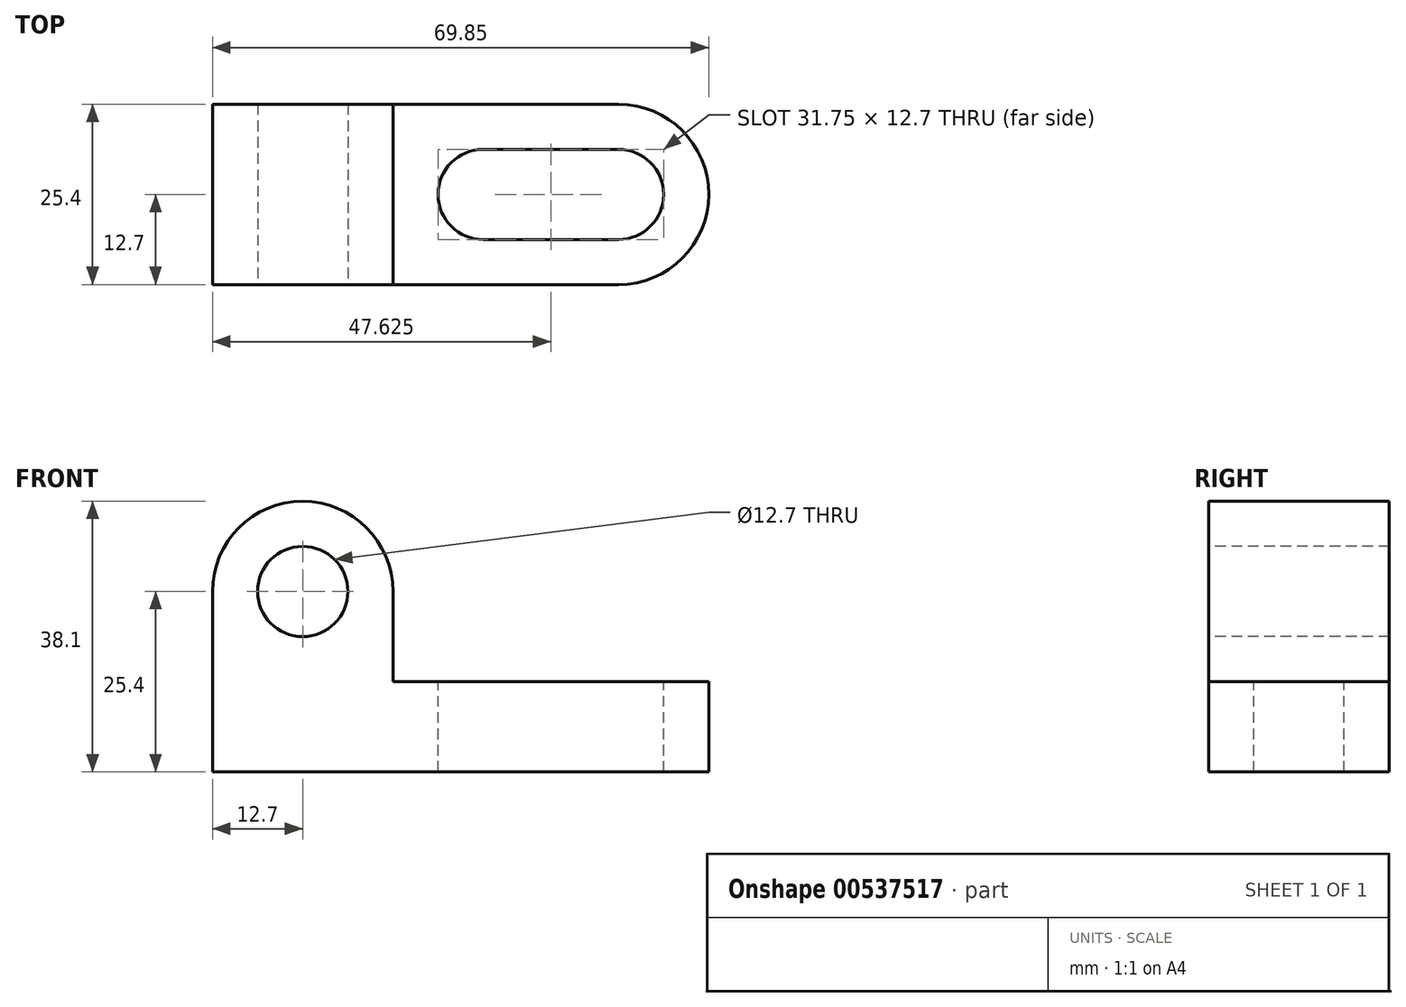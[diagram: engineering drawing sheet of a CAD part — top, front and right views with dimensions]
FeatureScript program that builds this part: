
annotation { "Feature Type Name" : "Feature", "Feature Type Description" : "" }
export const myFeature = defineFeature(function(context is Context, id is Id, definition is map)
    precondition{}
    {
        {
            var Q0;
            Q0=qCreatedBy(makeId("Front.planeOp"),FACE);
            var sketch = newSketch(context, id + "F0", { "sketchPlane" : qUnion([Q0])});
            skLineSegment(sketch, "E0", {"start": v(0, 0) * mm, "end": v(69.85, 0) * mm});
            skLineSegment(sketch, "E1", {"start": v(69.85, 0) * mm, "end": v(69.85, 38.1) * mm});
            skLineSegment(sketch, "E2", {"start": v(69.85, 38.1) * mm, "end": v(0, 38.1) * mm});
            skLineSegment(sketch, "E3", {"start": v(0, 38.1) * mm, "end": v(0, 0) * mm});
            skSolve(sketch);
        }
        {
            var Q0;
            Q0 = qSketchRegion(id + "F0", true);
            extrude(context, id + "F1", {"entities" : qUnion([Q0]), "depth" : 25.4 * mm, "offsetDistance" : 25.4 * mm});
        }
        {
            var Q0;
            Q0=makeQuery(id+"F1.opExtrude","CAP_FACE",FACE,{"disambiguationData":[OSD([sQuery(id+"F0.wireOp",EDGE,"E0"),sQuery(id+"F0.wireOp",EDGE,"E1"),sQuery(id+"F0.wireOp",EDGE,"E2"),sQuery(id+"F0.wireOp",EDGE,"E3")])],"isStart":false});
            var sketch = newSketch(context, id + "F2", { "sketchPlane" : qUnion([Q0])});
            skLineSegment(sketch, "E4", {"start": v(69.85, 0) * mm, "end": v(69.85, 12.7) * mm});
            skLineSegment(sketch, "E5", {"start": v(69.85, 12.7) * mm, "end": v(25.4, 12.7) * mm});
            skLineSegment(sketch, "E6", {"start": v(25.4, 12.7) * mm, "end": v(25.4, 38.1) * mm});
            skLineSegment(sketch, "E7", {"start": v(25.4, 38.1) * mm, "end": v(0, 38.1) * mm});
            skSolve(sketch);
        }
        {
            var Q0;
            Q0 = qSketchRegion(id + "F2", true);
            var Q1;
            {var subQ0=sQuery(id+"F2.wireOp",EDGE,"E5");Q1=makeQuery(id+"F2.imprint","IMPRINT",FACE,{"disambiguationData":[TD([[makeQuery(id+"F2.imprint","IMPRINT",EDGE,{"derivedFrom":subQ0}),-1.0]])]});}
            extrude(context, id + "F3", {"entities" : qUnion([Q0, Q1]), "operationType" : NewBodyOperationType.REMOVE, "oppositeDirection" : true, "depth" : 25.4 * mm, "offsetDistance" : 25.4 * mm});
        }
        {
            var Q0;
            Q0=makeQuery(id+"F1.opExtrude","CAP_FACE",FACE,{"disambiguationData":[OSD([sQuery(id+"F0.wireOp",EDGE,"E0"),sQuery(id+"F0.wireOp",EDGE,"E1"),sQuery(id+"F0.wireOp",EDGE,"E2"),sQuery(id+"F0.wireOp",EDGE,"E3")])],"isStart":false});
            var sketch = newSketch(context, id + "F4", { "sketchPlane" : qUnion([Q0])});
            skLineSegment(sketch, "E8", {"start": v(0, 38.1) * mm, "end": v(0, 25.4) * mm});
            skLineSegment(sketch, "E9", {"start": v(25.4, 38.1) * mm, "end": v(25.4, 25.4) * mm});
            skArc(sketch, "E10", {"start": v(25.4, 25.4) * mm, "mid": v(12.7, 38.1) * mm, "end": v(0, 25.4) * mm});
            skLineSegment(sketch, "E11", {"start": v(12.7, 38.1) * mm, "end": v(12.7, 31.75) * mm});
            skPoint(sketch, "E11.endSnap0", {"position": v(12.7, 38.1) * mm});
            skLineSegment(sketch, "E12", {"start": v(12.7, 0) * mm, "end": v(12.7, 19.05) * mm});
            skCircle(sketch, "E13", {"center": v(12.7, 25.4) * mm, "radius": 6.35 * mm});
            skSolve(sketch);
        }
        {
            var Q0;
            {var subQ0=sQuery(id+"F4.wireOp",EDGE,"E8");Q0=makeQuery(id+"F4.imprint","IMPRINT",FACE,{"disambiguationData":[TD([[makeQuery(id+"F4.imprint","IMPRINT",EDGE,{"derivedFrom":subQ0}),1.0]])]});}
            var Q1;
            {var subQ0=sQuery(id+"F4.wireOp",EDGE,"E9");Q1=makeQuery(id+"F4.imprint","IMPRINT",FACE,{"disambiguationData":[TD([[makeQuery(id+"F4.imprint","IMPRINT",EDGE,{"derivedFrom":subQ0}),1.0]])]});}
            var Q2;
            {var subQ0=sQuery(id+"F4.wireOp",EDGE,"E13");var subQ1=makeQuery(id+"F4.imprint","INTERSECT",VERTEX,{"derivedFrom":[sQuery(id+"F4.wireOp",EDGE,"E11"),subQ0]});Q2=makeQuery(id+"F4.imprint","IMPRINT",FACE,{"disambiguationData":[TD([[makeQuery(id+"F4.imprint","IMPRINT",EDGE,{"disambiguationData":[TD([[subQ1,-1.0]])],"derivedFrom":subQ0}),1.0]])]});}
            extrude(context, id + "F5", {"entities" : qUnion([Q0, Q1, Q2]), "operationType" : NewBodyOperationType.REMOVE, "oppositeDirection" : true, "depth" : 25.4 * mm, "offsetDistance" : 25.4 * mm});
        }
        {
            var Q0;
            Q0=makeQuery(id+"F3.boolean.opBoolean","COPY",FACE,{"derivedFrom":makeQuery(id+"F3.opExtrude","SWEPT_FACE",FACE,{"disambiguationData":[OSD([sQuery(id+"F2.wireOp",EDGE,"E5")])]})});
            var sketch = newSketch(context, id + "F6", { "sketchPlane" : qUnion([Q0])});
            skCircle(sketch, "E14", {"center": v(38.1, -12.7) * mm, "radius": 6.35 * mm});
            skCircle(sketch, "E15", {"center": v(57.15, -12.7) * mm, "radius": 6.35 * mm});
            skLineSegment(sketch, "E16", {"start": v(38.1, -6.35) * mm, "end": v(57.15, -6.35) * mm});
            skLineSegment(sketch, "E17", {"start": v(38.1, -19.05) * mm, "end": v(57.15, -19.05) * mm});
            skSolve(sketch);
        }
        {
            var Q0;
            {var subQ0=sQuery(id+"F6.wireOp",EDGE,"E14");var subQ1=makeQuery(id+"F6.imprint","INTERSECT",VERTEX,{"derivedFrom":[subQ0,sQuery(id+"F6.wireOp",EDGE,"E16")]});Q0=makeQuery(id+"F6.imprint","IMPRINT",FACE,{"disambiguationData":[TD([[makeQuery(id+"F6.imprint","IMPRINT",EDGE,{"disambiguationData":[TD([[subQ1,-1.0]])],"derivedFrom":subQ0}),1.0]])]});}
            var Q1;
            {var subQ0=sQuery(id+"F6.wireOp",EDGE,"E16");Q1=makeQuery(id+"F6.imprint","IMPRINT",FACE,{"disambiguationData":[TD([[makeQuery(id+"F6.imprint","IMPRINT",EDGE,{"derivedFrom":subQ0}),-1.0]])]});}
            var Q2;
            {var subQ0=sQuery(id+"F6.wireOp",EDGE,"E15");var subQ1=makeQuery(id+"F6.imprint","INTERSECT",VERTEX,{"derivedFrom":[subQ0,sQuery(id+"F6.wireOp",EDGE,"E16")]});Q2=makeQuery(id+"F6.imprint","IMPRINT",FACE,{"disambiguationData":[TD([[makeQuery(id+"F6.imprint","IMPRINT",EDGE,{"disambiguationData":[TD([[subQ1,-1.0]])],"derivedFrom":subQ0}),1.0]])]});}
            extrude(context, id + "F7", {"entities" : qUnion([Q0, Q1, Q2]), "operationType" : NewBodyOperationType.REMOVE, "oppositeDirection" : true, "depth" : 12.7 * mm, "offsetDistance" : 25.4 * mm});
        }
        {
            var Q0;
            Q0=makeQuery(id+"F3.boolean.opBoolean","COPY",FACE,{"derivedFrom":makeQuery(id+"F3.opExtrude","SWEPT_FACE",FACE,{"disambiguationData":[OSD([sQuery(id+"F2.wireOp",EDGE,"E5")])]})});
            var sketch = newSketch(context, id + "F8", { "sketchPlane" : qUnion([Q0])});
            skArc(sketch, "E18", {"start": v(57.15, -25.4) * mm, "mid": v(69.85, -12.7) * mm, "end": v(57.15, 0) * mm});
            skLineSegment(sketch, "E19", {"start": v(57.15, 0) * mm, "end": v(69.85, 0) * mm});
            skLineSegment(sketch, "E20", {"start": v(57.15, -12.7) * mm, "end": v(69.85, -12.7) * mm});
            skSolve(sketch);
        }
        {
            var Q0;
            Q0 = qSketchRegion(id + "F8", true);
            var Q1;
            {var subQ0=sQuery(id+"F8.wireOp",EDGE,"E19");Q1=makeQuery(id+"F8.imprint","IMPRINT",FACE,{"disambiguationData":[TD([[makeQuery(id+"F8.imprint","IMPRINT",EDGE,{"derivedFrom":subQ0}),1.0]])]});}
            var Q2;
            {var subQ0=sQuery(id+"F8.wireOp",EDGE,"E18");var subQ1=sQuery(id+"F2.wireOp",EDGE,"E5");var subQ2=makeQuery(id+"F3.boolean.opBoolean","COPY",EDGE,{"derivedFrom":makeQuery(id+"F3.opExtrude","CAP_EDGE",EDGE,{"disambiguationData":[OSD([subQ1])],"isStart":true})});var subQ3=makeQuery(id+"F8.imprint","INTERSECT",VERTEX,{"derivedFrom":[subQ2,subQ0]});Q2=makeQuery(id+"F8.imprint","IMPRINT",FACE,{"disambiguationData":[TD([[makeQuery(id+"F8.imprint","IMPRINT",EDGE,{"disambiguationData":[TD([[subQ3,-1.0]])],"derivedFrom":subQ0}),-1.0]])]});}
            extrude(context, id + "F9", {"entities" : qUnion([Q0, Q1, Q2]), "operationType" : NewBodyOperationType.REMOVE, "oppositeDirection" : true, "depth" : 12.7 * mm, "offsetDistance" : 25.4 * mm});
        }
    });
